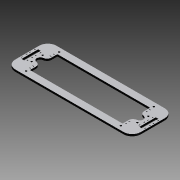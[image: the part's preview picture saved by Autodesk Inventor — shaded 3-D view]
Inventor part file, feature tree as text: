
AUTODESK INVENTOR PART (.ipt)
format: ipt  version: 2013 (Build 170138000, 138)  size: 310,272 bytes
history: native  units: mm
features: extrude x4, sketch x4, mirror x3, fillet x1
ambient origin geometry x8: Origin, YZ Plane, XZ Plane, XY Plane, X Axis, Y Axis, Z Axis, Center Point
bodies: Solid1 (feature_tree)
feature tree (12):
  extrude  "Extrusion1"  Depth=70.0mm
  fillet  "Fillet1"  Radius=30.0mm
  extrude  "Extrusion2"  Depth=4.0mm
  mirror  "Mirror1"
  mirror  "Mirror2"
  extrude  "Extrusion3"  Depth=10.0mm
  mirror  "Mirror3"
  extrude  "Extrusion4"  Depth=16.0mm
  sketch  "Sketch1"  dims[d0=130.0mm d1=70.0mm d2=30.0mm]
  sketch  "Sketch2"  dims[d3=20.0mm d4=4.0mm]
  sketch  "Sketch3"  dims[d5=10.0mm d6=10.0mm]
  sketch  "Sketch5"  dims[d7=145.0mm d8=16.0mm d9=16.0mm d10=16.0mm d11=7.5mm d13=24.0mm d14=11.5mm d15=183.0mm d16=5.715mm d17=0.0mm d18=5.0mm d19=2.0mm d20=25.0mm d21=8.0mm d23=1.5mm d24=4.0mm d25=5.0mm d26=7.5mm d27=6.477mm d28=0.0mm d29=15.0mm d31=10.0mm d32=7.5mm d34=20.0mm d35=10.0mm d36=10.0mm d37=0.0mm d38=18.0mm d42=10.0mm d43=0.0mm]
